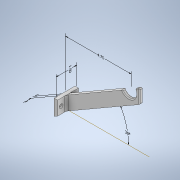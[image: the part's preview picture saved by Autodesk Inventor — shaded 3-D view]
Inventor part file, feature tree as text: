
AUTODESK INVENTOR PART (.ipt)
format: ipt  version: 2021.1 (Build 251245010, 245A)  size: 374,784 bytes
history: native  units: in
note: dims shown in document units (in); Inventor stores cm internally (conversion verified against a paired STEP export)
features: other x5, sketch x5, extrude x4, fillet x4, hole x1
ambient origin geometry x8: Origin, YZ Plane, XZ Plane, XY Plane, X Axis, Y Axis, Z Axis, Center Point
bodies: Solid2 (feature_tree)
feature tree (19):
  other  "Annotations"
  extrude  "Extrusion3"  Depth=0.25in
  extrude  "Extrusion4"  TaperAngle=30.0deg  [1 undecoded]
  sketch  "Sketch7"  dims[d26=1.075in d29=0.25in]
  extrude  "Extrusion5"  Depth=0.25in
  hole  "Hole3"  [1 undecoded]
  fillet  "Fillet3"  [1 undecoded]
  fillet  "Fillet4"  [1 undecoded]
  fillet  "Fillet5"  Radius=0.25in
  fillet  "Fillet6"  Radius=0.25in
  extrude  "Extrusion6"  Depth=0.0625in
  sketch  "Sketch5"  dims[d21=1.0in d22=0.25in]
  sketch  "Sketch6"  dims[d23=1.5in d24=0.0in d25=30.0deg]
  sketch  "Sketch8"  dims[d30=4.75in d31=0.25in d32=0.0in d33=0.0in d34=0.25in d35=0.25in]
  sketch  "Sketch9"  dims[d47=1.5in d48=0.0in d49=0.15in d50=0.75in d51=0.279in d52=0.25in d53=0.5635in d54=1.0in d55=0.8108in d65=0.0625in d66=0.0625in d67=0.0625in d68=0.125in d72=0.05in d73=0.0in d56=0.2085in d57=0.331in d58=1.5in d59=2.3174in d60=30.0deg d69=4.75in d70=0.3005in d71=0.25in]
  other  "Linear Dimension 1"
  other  "Angular Dimension 1"
  other  "Linear Dimension 2"
  other  "Linear Dimension 3"
note: 4 required parameter values undecoded (feature->parameter linkage not recoverable at this tier; creation-order binding heuristic only, values carry confidence <= 0.55)
